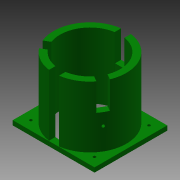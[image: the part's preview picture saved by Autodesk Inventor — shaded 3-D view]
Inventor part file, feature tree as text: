
AUTODESK INVENTOR PART (.ipt)
format: ipt  version: 2013 (Build 170138000, 138)  size: 310,272 bytes
history: native  units: mm
features: sketch x15, extrude x12, other x5, hole x3, pattern_circular x1
ambient origin geometry x8: Origin, YZ Plane, XZ Plane, XY Plane, X Axis, Y Axis, Z Axis, Center Point
feature tree (36):
  other  "ソリッド1"
  extrude  "押し出し1"  Depth=26.0mm
  extrude  "押し出し2"  Depth=20.0mm
  hole  "穴1"  [1 undecoded]
  pattern_circular  "円形状パターン1"  [2 undecoded]
  other  "作業平面21"
  other  "作業平面18"
  hole  "穴2"  [1 undecoded]
  other  "作業平面17"
  extrude  "押し出し4"  Depth=10.8mm
  extrude  "押し出し5"  Depth=145.0mm TaperAngle=0.0deg
  extrude  "押し出し6"  Depth=30.0mm TaperAngle=360.0deg
  extrude  "押し出し7"  Depth=19.5mm
  other  "作業平面16"
  extrude  "押し出し8"  Depth=4.7mm
  extrude  "押し出し9"  Depth=50.6mm
  extrude  "押し出し10"  Depth=3.0mm
  extrude  "押し出し11"  Depth=3.0mm
  extrude  "押し出し12"  Depth=5.1mm
  hole  "穴3"  [1 undecoded]
  extrude  "押し出し13"  Depth=3.0mm
  sketch  "スケッチ1"
  sketch  "スケッチ2"
  sketch  "スケッチ3"
  sketch  "スケッチ6"
  sketch  "スケッチ7"
  sketch  "スケッチ8"
  sketch  "スケッチ9"
  sketch  "スケッチ10"
  sketch  "スケッチ12"
  sketch  "スケッチ13"
  sketch  "スケッチ14"
  sketch  "スケッチ15"
  sketch  "スケッチ16"
  sketch  "スケッチ17"
  sketch  "スケッチ18"
note: 5 required parameter values undecoded (feature->parameter linkage not recoverable at this tier; creation-order binding heuristic only, values carry confidence <= 0.55)
